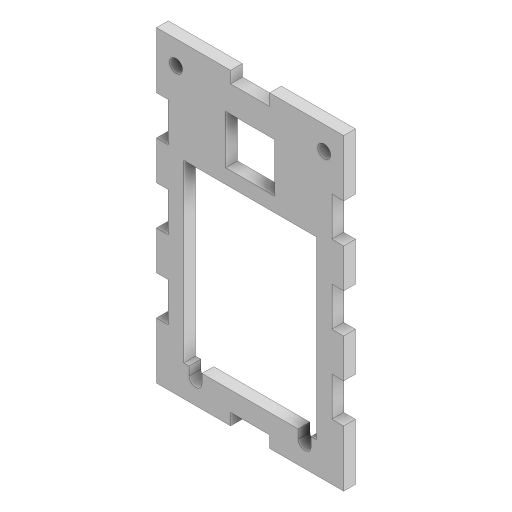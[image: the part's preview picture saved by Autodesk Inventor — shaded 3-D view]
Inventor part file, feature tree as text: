
AUTODESK INVENTOR PART (.ipt)
format: ipt  version: 2023.3 (Build 273359000, 359)  size: 185,344 bytes
history: native  units: mm
features: extrude x1, sketch x1
ambient origin geometry x8: Origin, YZ Plane, XZ Plane, XY Plane, X Axis, Y Axis, Z Axis, Center Point
bodies: Solid1 (feature_tree)
feature tree (2):
  extrude  "Extrusion1"  Depth=3.3mm
  sketch  "Sketch1"  dims[d0=3.3mm d1=3.3mm d2=28.0mm d3=14.0mm d4=3.3mm d5=3.3mm d6=38.0mm d7=19.0mm d8=34.0mm d9=44.0mm d10=3.25mm d11=20.0mm d12=5.0mm d13=10.0mm d14=9.0mm d15=26.0mm d16=7.0mm d17=1.0mm d18=3.0mm d19=10.0mm d20=10.0mm d21=3.0mm d22=10.0mm d23=3.0mm d24=20.0mm d26=20.0mm d27=10.0mm d29=10.0mm d31=20.0mm d33=20.0mm d34=10.0mm d36=10.0mm d38=3.0mm d39=10.0mm d40=20.0mm d42=20.0mm d43=10.0mm d45=10.0mm d47=20.0mm d49=20.0mm d50=10.0mm d52=10.0mm d54=3.0mm d55=0.0mm d56=12.5mm d57=12.5mm]
